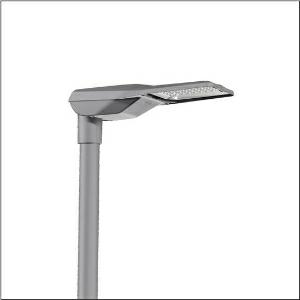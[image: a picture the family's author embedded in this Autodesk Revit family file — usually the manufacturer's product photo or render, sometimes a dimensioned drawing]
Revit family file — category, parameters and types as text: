
# Revit family: streetlight_sl_21_iq_mini___st0_8a_5xe2c31g08hb_2845
name_source: partatom
category: Lighting Fixtures
units: mm (PartAtom-declared; Revit-internal decimal feet)

## family parameters
Cut with Voids When Loaded = No
Host = Face
Light Source = No
Part Type = Normal
Room Calculation Point = No
Round Connector Dimension = Use Diameter
Shared = No

## types (1)
- --- (1 x LED, 9450 lm, 70.9 W, 3000K)
    Apparent Load = 71 VA
    CIE Flux Codes = 38 75 97 100 100
    Color Rendering = 70
    Color Temperature = 3000K
    Default Elevation = 1800 mm
    Description = Streetlight SL 21 iQ mini, mast luminaire, primary light control with lens, of PMMA, primary optical cover: cover, of toughened safety glass, transparent, light distribution: ST0.8a, light emission: direct distribution, primary light characteristic: asymmetric, installation type: post-top, side-entry, LED, High Power LED, rated luminous flux: 9.450lm, luminous efficacy: 133lm/W, light colour: 730, colour temperature: 3000K, control gear: iQ Street-Remote, control: Street-Remote, Auto-Match, Temp-Guard, Lumen-Switch, Night-Set, Smart-Wire, Light-Fading, Desk-Remote (wireless, voltage-free reading and setting of iQ features in the workshop via application-optimized NFC function/RFID function), optimised constant luminous flux control (CLO 2.0), pre-setting: linear dimming characteristic, mains connection: 220..240V, AC, 50/60Hz, start of lifetime: 71W, end of service life: 75W, reduction: 31W, luminaire housing, of diecast aluminium, powder-coated, SITECO metallic grey (DB 702S), corrosivity category C5 high according to DIN EN ISO 12944, please order mast flange separately, inclination adjustable: 0°, 5°, 10°, 15°, sealing non-destructively replaceable, multi-level sealing system, length: 628mm, width: 235mm, height: 110mm, mast flange for spigot size: 42mm (side-entry): 5XC10008XM4, 60/48mm (side-entry/post-top): 5XC10108XM2, 76/60mm (side-entry/post-top): 5XC10108XM1, mounting height: 4..8m, protection rating (complete): IP66, insulation class (complete): insulation class II (safety insulation), certification: CE, ENEC, ENEC+, VDE, impact resistance: IK10, permissible operating ambient temperature for outdoor applications: -40..+50°C, standard-compliant lighting for roads and squares, packaging unit: 1 piece

Light Distribution: ST0.8a
    Height = 110 mm
    Lamp = 1 x LED
    Lamp Light Flux = 9450 lm
    Lamp Power = 70.9 W
    Lamp count = 1
    Length = 625 mm
    Luminous efficacy = 133 lm/W
    Manufacturer = Siteco
    ModVariant = No
    Model = 5XE2C31G08HB
    Number of Poles = 1
    OnlyDefault = Yes
    Power Factor = 1
    Product Name = Streetlight SL 21 iQ mini | ST0.8a
    Product group = mast luminaire | pylon top
    ProductGroupID = 6100
    Protection Class = Protection class II
    Protection Degree = IP 66
    RLX_Detail_Level = 1
    RLX_Emergency_Light_Flux = 0 lm
    RLX_Emergency_Type = 0
    RLX_Emergency_Type_DB = No
    RlxData = <blob elided: 26353 chars, md5=50be8ab0>
    Socket = socket
    Standby Power = 0 W
    System Light Flux = 9450 lm
    System Power = 71 W
    Type Comments = factory setting: luminous flux: 100 % | dim-lin: 254 | 711 mA
    Type Image = l_1003519.jpg
    URL = http://relux.com
    VarID = @adj_156881
    Voltage = 0 V
    Weight = 0.00 kg
    Width = 234 mm

## geometry (parser evidence)
native form markers: Blend x4, Sweep x10
no freeform markers — native parametric forms only
